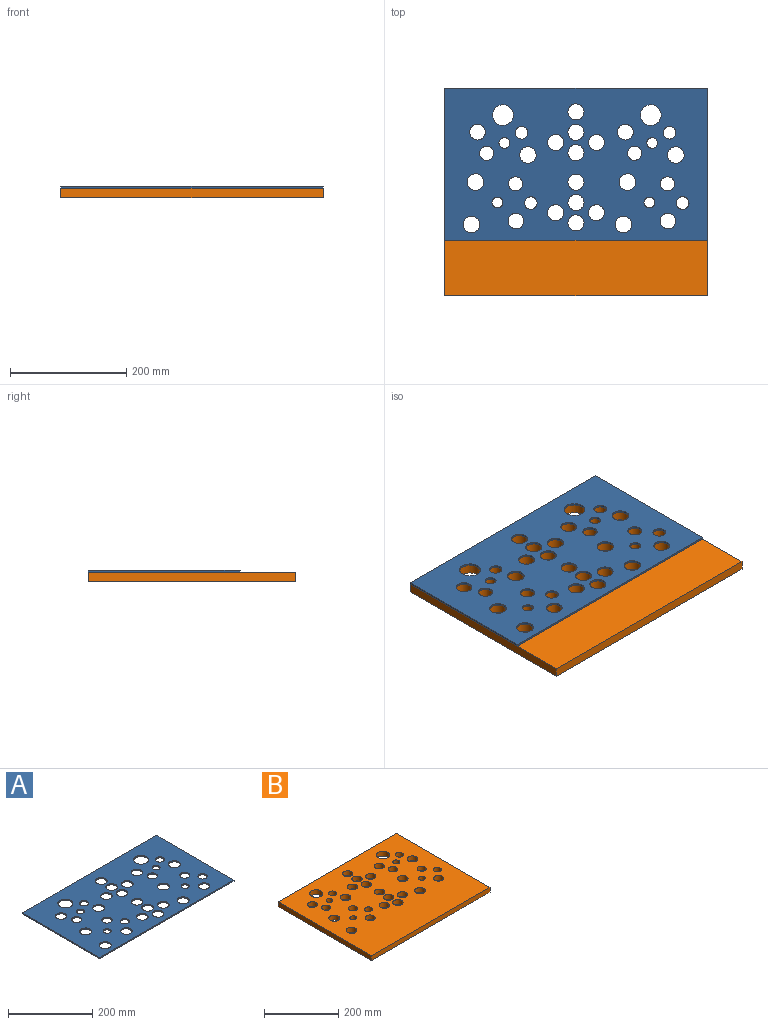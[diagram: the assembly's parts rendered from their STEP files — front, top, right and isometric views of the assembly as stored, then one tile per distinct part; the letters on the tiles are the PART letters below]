
ASSEMBLY  parts=2 mates=1
PART A: 40 faces, bbox 450.9x260.4x3.2 mm
  f0: plane 260.35x3.18mm, normal (-1,0,0), area 826.6mm2, adj f1,f3,f4,f5
  f1: plane 450.85x3.18mm, normal (0,-1,0), area 1431.4mm2, adj f0,f2,f4,f5
  f2: plane 260.35x3.18mm, normal (1,0,0), area 826.6mm2, adj f1,f3,f4,f5
  f3: plane 450.85x3.18mm, normal (0,1,0), area 1431.4mm2, adj f0,f2,f4,f5
  f4: plane 450.85x260.35mm, normal (0,0,1), area 98826.8mm2, adj f0,f1,f2,f3,f6,f7,f8,f9
  f5: plane 450.85x260.35mm, normal (0,0,-1), area 98826.8mm2, adj f0,f1,f2,f3,f6,f7,f8,f9
  f6: cylinder r=14.27mm len=28.54mm, axis (0,0,1), area 284.7mm2, adj f4,f5
  f7: cylinder r=14.27mm len=28.54mm, axis (0,0,1), area 284.7mm2, adj f4,f5
  f8: cylinder r=9.28mm len=18.57mm, axis (0,0,1), area 185.2mm2, adj f4,f5
  f9: cylinder r=12.19mm len=24.39mm, axis (0,0,1), area 243.3mm2, adj f4,f5
  f10: cylinder r=13.5mm len=27.01mm, axis (0,0,1), area 269.4mm2, adj f4,f5
  f11: cylinder r=9.28mm len=18.57mm, axis (0,0,1), area 185.2mm2, adj f4,f5
  f12: cylinder r=14.27mm len=28.54mm, axis (0,0,1), area 284.7mm2, adj f4,f5
  f13: cylinder r=14.27mm len=28.54mm, axis (0,0,1), area 284.7mm2, adj f4,f5
  f14: cylinder r=10.85mm len=21.71mm, axis (0,0,1), area 216.5mm2, adj f4,f5
  f15: cylinder r=13.5mm len=27.01mm, axis (0,0,1), area 269.4mm2, adj f4,f5
  f16: cylinder r=10.85mm len=21.71mm, axis (0,0,1), area 216.5mm2, adj f4,f5
  f17: cylinder r=12.19mm len=24.39mm, axis (0,0,1), area 243.3mm2, adj f4,f5
  f18: cylinder r=9.26mm len=18.52mm, axis (0,0,1), area 184.7mm2, adj f4,f5
  f19: cylinder r=17.81mm len=35.63mm, axis (0,0,1), area 355.4mm2, adj f4,f5
  f20: cylinder r=14.25mm len=28.5mm, axis (0,0,1), area 284.3mm2, adj f4,f5
  f21: cylinder r=10.86mm len=21.72mm, axis (0,0,1), area 216.6mm2, adj f4,f5
  f22: cylinder r=17.81mm len=35.63mm, axis (0,0,1), area 355.4mm2, adj f4,f5
  f23: cylinder r=10.86mm len=21.72mm, axis (0,0,1), area 216.6mm2, adj f4,f5
  f24: cylinder r=14.25mm len=28.5mm, axis (0,0,1), area 284.3mm2, adj f4,f5
  f25: cylinder r=12.2mm len=24.41mm, axis (0,0,1), area 243.5mm2, adj f4,f5
  f26: cylinder r=9.26mm len=18.52mm, axis (0,0,1), area 184.7mm2, adj f4,f5
  f27: cylinder r=12.2mm len=24.41mm, axis (0,0,1), area 243.5mm2, adj f4,f5
  f28: cylinder r=13.51mm len=27.03mm, axis (0,0,1), area 269.6mm2, adj f4,f5
  f29: cylinder r=13.51mm len=27.03mm, axis (0,0,1), area 269.6mm2, adj f4,f5
  f30: cylinder r=13.82mm len=27.64mm, axis (0,0,1), area 275.7mm2, adj f4,f5
  f31: cylinder r=13.82mm len=27.64mm, axis (0,0,1), area 275.7mm2, adj f4,f5
  f32: cylinder r=13.82mm len=27.64mm, axis (0,0,1), area 275.7mm2, adj f4,f5
  f33: cylinder r=13.82mm len=27.64mm, axis (0,0,1), area 275.7mm2, adj f4,f5
  f34: cylinder r=13.82mm len=27.64mm, axis (0,0,1), area 275.7mm2, adj f4,f5
  f35: cylinder r=13.82mm len=27.64mm, axis (0,0,1), area 275.7mm2, adj f4,f5
  f36: cylinder r=13.82mm len=27.64mm, axis (0,0,1), area 275.7mm2, adj f4,f5
  f37: cylinder r=13.82mm len=27.64mm, axis (0,0,1), area 275.7mm2, adj f4,f5
  f38: cylinder r=13.82mm len=27.64mm, axis (0,0,1), area 275.7mm2, adj f4,f5
  f39: cylinder r=13.82mm len=27.64mm, axis (0,0,1), area 275.7mm2, adj f4,f5
PART B: 40 faces, bbox 450.9x355.6x15.9 mm
  f0: plane 450.85x15.88mm, normal (0,1,0), area 7157.2mm2, adj f1,f3,f4,f5
  f1: plane 355.6x15.88mm, normal (-1,0,0), area 5645.2mm2, adj f0,f2,f4,f5
  f2: plane 450.85x15.88mm, normal (0,-1,0), area 7157.2mm2, adj f1,f3,f4,f5
  f3: plane 355.6x15.88mm, normal (1,0,0), area 5645.2mm2, adj f0,f2,f4,f5
  f4: plane 450.85x355.6mm, normal (0,0,1), area 141770.2mm2, adj f0,f1,f2,f3,f6,f7,f8,f9
  f5: plane 450.85x355.6mm, normal (0,0,-1), area 141770.2mm2, adj f0,f1,f2,f3,f6,f7,f8,f9
  f6: cylinder r=14.27mm len=28.54mm, axis (0,0,1), area 1423.3mm2, adj f4,f5
  f7: cylinder r=14.27mm len=28.54mm, axis (0,0,1), area 1423.3mm2, adj f4,f5
  f8: cylinder r=9.28mm len=18.57mm, axis (0,0,1), area 926mm2, adj f4,f5
  f9: cylinder r=12.19mm len=24.39mm, axis (0,0,1), area 1216.3mm2, adj f4,f5
  f10: cylinder r=13.5mm len=27.01mm, axis (0,0,1), area 1347mm2, adj f4,f5
  f11: cylinder r=9.28mm len=18.57mm, axis (0,0,1), area 926mm2, adj f4,f5
  f12: cylinder r=14.27mm len=28.54mm, axis (0,0,1), area 1423.3mm2, adj f4,f5
  f13: cylinder r=14.27mm len=28.54mm, axis (0,0,1), area 1423.3mm2, adj f4,f5
  f14: cylinder r=10.85mm len=21.71mm, axis (0,0,1), area 1082.6mm2, adj f4,f5
  f15: cylinder r=13.5mm len=27.01mm, axis (0,0,1), area 1347mm2, adj f4,f5
  f16: cylinder r=10.85mm len=21.71mm, axis (0,0,1), area 1082.6mm2, adj f4,f5
  f17: cylinder r=12.19mm len=24.39mm, axis (0,0,1), area 1216.3mm2, adj f4,f5
  f18: cylinder r=9.26mm len=18.52mm, axis (0,0,1), area 923.5mm2, adj f4,f5
  f19: cylinder r=17.81mm len=35.63mm, axis (0,0,1), area 1776.9mm2, adj f4,f5
  f20: cylinder r=14.25mm len=28.5mm, axis (0,0,1), area 1421.3mm2, adj f4,f5
  f21: cylinder r=10.86mm len=21.72mm, axis (0,0,1), area 1083.1mm2, adj f4,f5
  f22: cylinder r=17.81mm len=35.63mm, axis (0,0,1), area 1776.9mm2, adj f4,f5
  f23: cylinder r=10.86mm len=21.72mm, axis (0,0,1), area 1083.1mm2, adj f4,f5
  f24: cylinder r=14.25mm len=28.5mm, axis (0,0,1), area 1421.3mm2, adj f4,f5
  f25: cylinder r=12.2mm len=24.41mm, axis (0,0,1), area 1217.4mm2, adj f4,f5
  f26: cylinder r=9.26mm len=18.52mm, axis (0,0,1), area 923.5mm2, adj f4,f5
  f27: cylinder r=12.2mm len=24.41mm, axis (0,0,1), area 1217.4mm2, adj f4,f5
  f28: cylinder r=13.51mm len=27.03mm, axis (0,0,1), area 1347.8mm2, adj f4,f5
  f29: cylinder r=13.51mm len=27.03mm, axis (0,0,1), area 1347.8mm2, adj f4,f5
  f30: cylinder r=13.82mm len=27.64mm, axis (0,0,1), area 1378.4mm2, adj f4,f5
  f31: cylinder r=13.82mm len=27.64mm, axis (0,0,1), area 1378.4mm2, adj f4,f5
  f32: cylinder r=13.82mm len=27.64mm, axis (0,0,1), area 1378.4mm2, adj f4,f5
  f33: cylinder r=13.82mm len=27.64mm, axis (0,0,1), area 1378.4mm2, adj f4,f5
  f34: cylinder r=13.82mm len=27.64mm, axis (0,0,1), area 1378.4mm2, adj f4,f5
  f35: cylinder r=13.82mm len=27.64mm, axis (0,0,1), area 1378.4mm2, adj f4,f5
  f36: cylinder r=13.82mm len=27.64mm, axis (0,0,1), area 1378.4mm2, adj f4,f5
  f37: cylinder r=13.82mm len=27.64mm, axis (0,0,1), area 1378.4mm2, adj f4,f5
  f38: cylinder r=13.82mm len=27.64mm, axis (0,0,1), area 1378.4mm2, adj f4,f5
  f39: cylinder r=13.82mm len=27.64mm, axis (0,0,1), area 1378.4mm2, adj f4,f5
PLACE A t=(225.17,178.08,-15.23)mm
PLACE B t=(225.17,178.08,-15.23)mm fixed
MATE fastened B.f4 <-> A.f5  axis (0,0,1) through (450.6,355.88,0.65)mm
